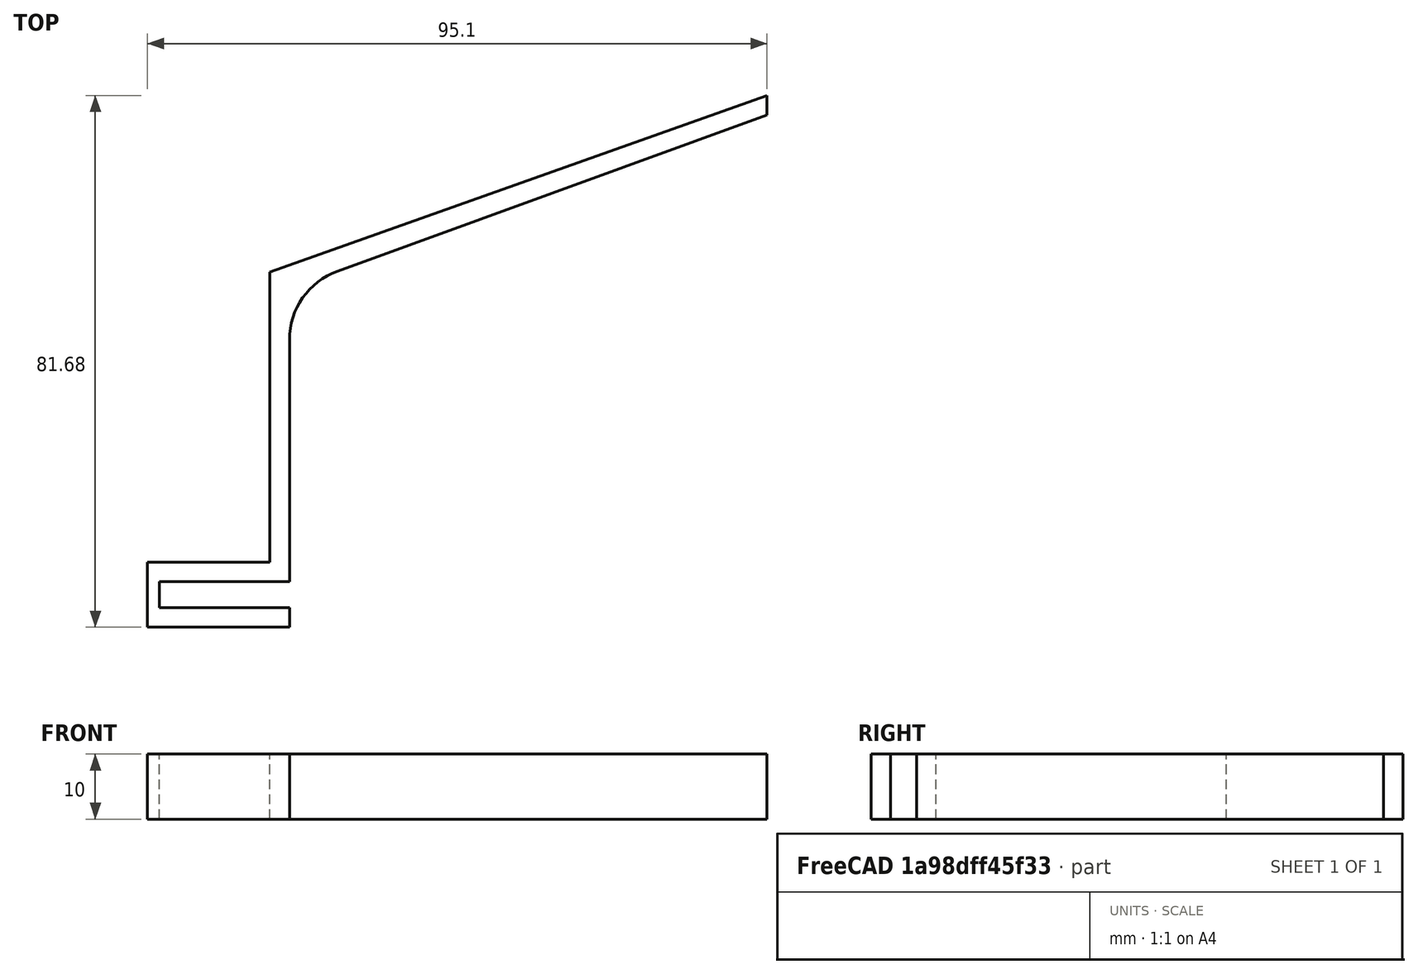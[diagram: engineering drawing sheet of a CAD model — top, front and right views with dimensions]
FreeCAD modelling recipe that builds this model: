
FCSTD DOCUMENT  (FreeCAD 0.22R38261 (Git))
Label: профиль лодки
License: All rights reserved
LicenseURL: https://en.wikipedia.org/wiki/All_rights_reserved
objects: Sketcher::SketchObject×1, PartDesign::Pad×1, PartDesign::Body×1
note: 5 computed .brp shape members not serialized (recipe doc carries the construction recipe); baked Part::Feature solids carry a one-line shape summary decoded from their .brp

FEATURE [Sketcher::SketchObject] Sketch
  AttachmentSupport = -> [XY_Plane]
  FullyConstrained = false
  MapMode = 5
  sketch-geometry (16):
    g0: LineSegment StartX=0 StartY=0 StartZ=0 EndX=20 EndY=0 EndZ=0
    g1: LineSegment StartX=0 StartY=-4 StartZ=0 EndX=20 EndY=-4 EndZ=0
    g2: GeomPoint X=0 Y=-4 Z=0
    g3: LineSegment StartX=20 StartY=-4 StartZ=0 EndX=20 EndY=-7 EndZ=0
    g4: LineSegment StartX=20 StartY=-7 StartZ=0 EndX=-1.80496 EndY=-7 EndZ=0
    g5: LineSegment StartX=-1.80496 StartY=-7 StartZ=0 EndX=-1.80496 EndY=3 EndZ=0
    g6: LineSegment StartX=-1.80496 StartY=3 StartZ=0 EndX=17 EndY=3 EndZ=0
    g7: LineSegment StartX=20 StartY=0 StartZ=0 EndX=20 EndY=37.1541 EndZ=0
    g8: LineSegment StartX=27.3727 StartY=47.6835 StartZ=0 EndX=93.296 EndY=71.6776 EndZ=0
    g9: ArcOfCircle CenterX=31.2051 CenterY=37.1541 CenterZ=0 NormalX=0 NormalY=0 NormalZ=1 AngleXU=0 Radius=11.2051 StartAngle=1.91986 EndAngle=3.14159
    g10: GeomPoint X=20 Y=45 Z=0
    g11: LineSegment StartX=17 StartY=3 StartZ=0 EndX=17 EndY=47.5547 EndZ=0
    g12: LineSegment StartX=93.296 StartY=71.6776 StartZ=0 EndX=93.296 EndY=74.6776 EndZ=0
    g13: LineSegment StartX=17 StartY=47.5547 StartZ=0 EndX=93.296 EndY=74.6776 EndZ=0
    g14: LineSegment StartX=0 StartY=0 StartZ=0 EndX=0 EndY=0 EndZ=0
    g15: LineSegment StartX=0 StartY=-4 StartZ=0 EndX=0 EndY=0 EndZ=0
  constraints (39):
    c: PointOnObject(g2,g-2)
    c: Distance(g-1,g2) = 4
    c: Horizontal(g1)
    c: PointOnObject(g2,g1)
    c: PointOnObject(g-1,g0)
    c: Horizontal(g0)
    c: Coincident(g3,g1)
    c: Vertical(g3)
    c: Coincident(g4,g3)
    c: Horizontal(g4)
    c: Coincident(g5,g4)
    c: Vertical(g5)
    c: Horizontal(g6)
    c: Distance(g3) = 3
    c: Coincident(g5,g6)
    c: DistanceY(g0,g5) = 3
    c: DistanceX(g1,g1) = 20
    c: DistanceX(g0,g0) = 20
    c: Coincident(g7,g0)
    c: Vertical(g7)
    c: DistanceY(g7,g10) = 45
    c: Distance(g8,g10) = 78
    c: PointOnObject(g10,g7)
    c: PointOnObject(g10,g8)
    c: Tangent(g7,g9) = 1.5708
    c: Tangent(g8,g9) = 1.5708
    c: Angle(g7,g8) = 1.91986
    c: Coincident(g11,g6)
    c: Vertical(g11)
    c: Coincident(g12,g8)
    c: Vertical(g12)
    c: DistanceY(g12,g12) = 3
    c: Coincident(g13,g11)
    c: Coincident(g13,g12)
    c: DistanceX(g6,g0) = 3
    c: Coincident(g14,g0)
    c: Coincident(g15,g1)
    c: Coincident(g15,g14)
    c: Vertical(g15)
FEATURE [PartDesign::Pad] Pad
  Direction = (0,0,1)
  Length = 10
  Length2 = 10
  Profile = -> Sketch
  ReferenceAxis = -> Sketch [N_Axis]
  Suppressed = false
  Type = 0
FEATURE [PartDesign::Body] Body
  AllowCompound = false
  Group = -> [Sketch,Pad]
  Origin = -> Origin
  Tip = -> Pad
